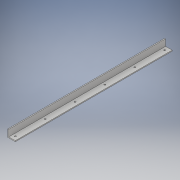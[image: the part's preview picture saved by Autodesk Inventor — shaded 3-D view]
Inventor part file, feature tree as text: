
AUTODESK INVENTOR PART (.ipt)
format: ipt  version: 2018 (Build 220112000, 112)  size: 121,344 bytes
history: native  units: in
note: dims shown in document units (in); Inventor stores cm internally (conversion verified against a paired STEP export)
features: extrude x2, sketch x2
ambient origin geometry x8: Origin, YZ Plane, XZ Plane, XY Plane, X Axis, Y Axis, Z Axis, Center Point
bodies: Solid1 (feature_tree)
feature tree (4):
  extrude  "Extrusion1"  Depth=1.0in
  extrude  "Extrusion2"  Depth=0.125in
  sketch  "Sketch1"  dims[d0=0.125in d1=1.0in]
  sketch  "Sketch2"  dims[d2=1.0in d3=0.125in d4=21.0in d5=0.0in d6=0.5in d7=0.5in d8=4.0in d9=4.0in d10=4.0in d11=4.0in d12=4.0in d13=0.2031in d14=21.0in d15=0.0in]
